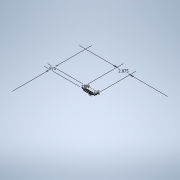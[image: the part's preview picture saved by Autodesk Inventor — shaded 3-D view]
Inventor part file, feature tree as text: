
AUTODESK INVENTOR PART (.ipt)
format: ipt  version: 2020 (Build 240168000, 168)  size: 134,656 bytes
history: native  units: in
note: dims shown in document units (in); Inventor stores cm internally (conversion verified against a paired STEP export)
features: sketch x1, extrude x1, hole x1, fillet x1
ambient origin geometry x8: Origin, YZ Plane, XZ Plane, XY Plane, X Axis, Y Axis, Z Axis, Center Point
bodies: Solid1 (feature_tree)
feature tree (4):
  sketch  "Sketch1"  dims[d0=2.875in d1=0.875in d2=0.75in d3=0.75in d4=0.5in d5=0.125in d6=0.0in d7=0.125in d8=0.125in d9=0.125in d10=0.125in d11=0.129in d12=0.75in d13=0.219in d14=0.0625in d15=0.5635in d16=1.0in d17=0.8108in d19=0.125in]
  extrude  "Extrusion1"  Depth=0.875in
  hole  "Hole1"  [1 undecoded]
  fillet  "Fillet2"  Radius=0.75in
note: 1 required parameter value undecoded (feature->parameter linkage not recoverable at this tier; creation-order binding heuristic only, values carry confidence <= 0.55)
